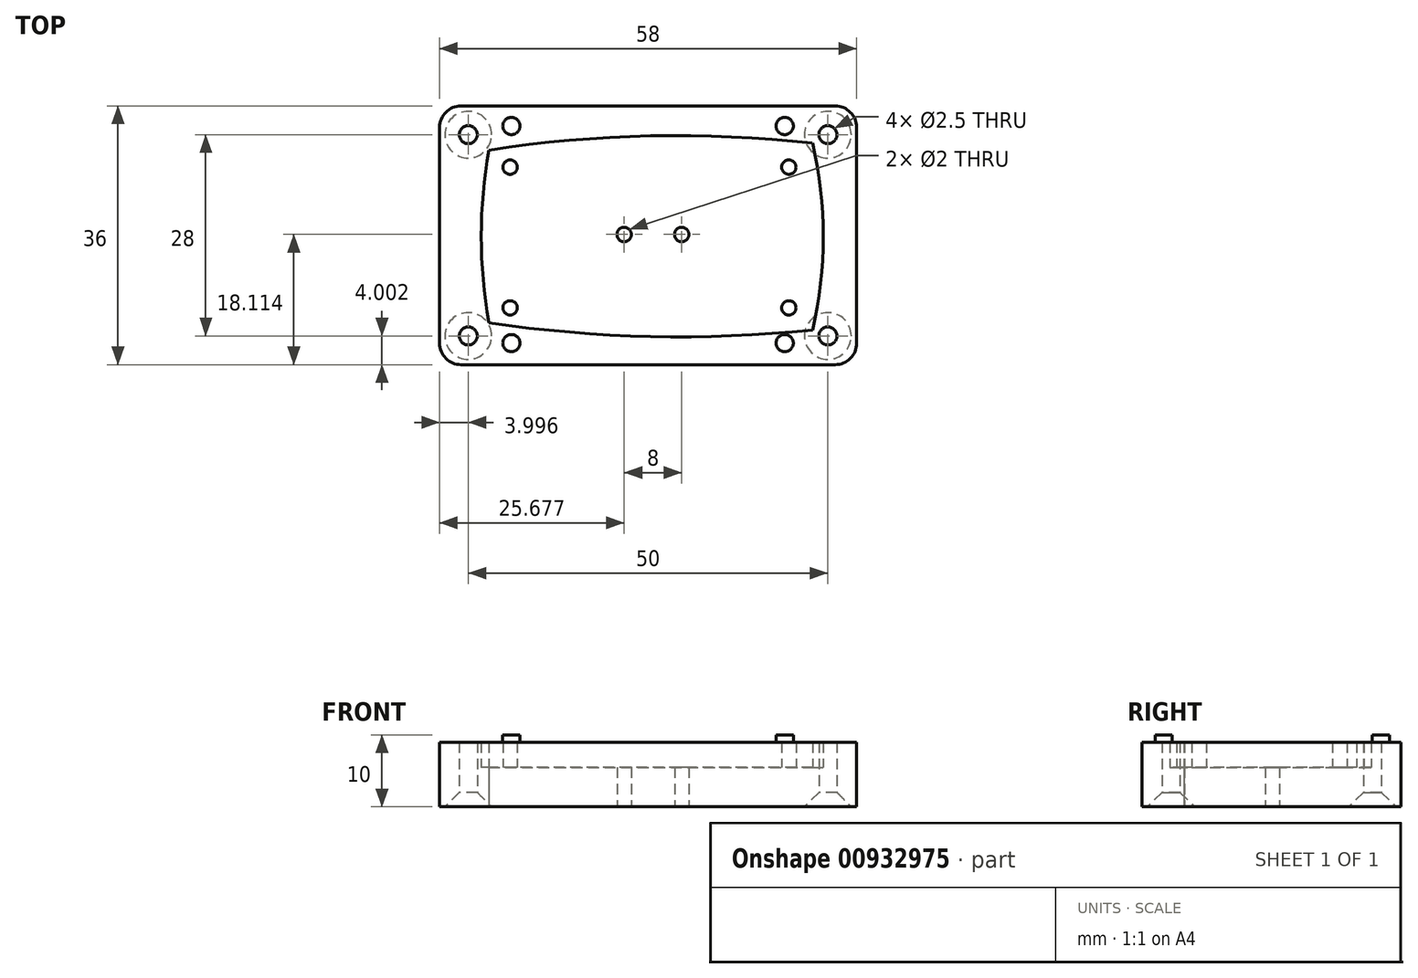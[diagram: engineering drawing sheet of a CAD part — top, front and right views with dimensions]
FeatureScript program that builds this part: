
annotation { "Feature Type Name" : "Feature", "Feature Type Description" : "" }
export const myFeature = defineFeature(function(context is Context, id is Id, definition is map)
    precondition{}
    {
        {
            var Q0;
            Q0=qCreatedBy(makeId("Top.planeOp"),FACE);
            var sketch = newSketch(context, id + "F0", { "sketchPlane" : qUnion([Q0])});
            skLineSegment(sketch, "E0", {"start": v(-0.01, 0.02) * mm, "end": v(-0.01, 24.02) * mm});
            skLineSegment(sketch, "E1", {"start": v(44.98, -1) * mm, "end": v(44.98, 25) * mm});
            skLineSegment(sketch, "E2", {"start": v(-0.01, 24.02) * mm, "end": v(44.98, 25) * mm});
            skLineSegment(sketch, "E3", {"start": v(-0.01, 0.02) * mm, "end": v(44.98, -1) * mm});
            skArc(sketch, "E4", {"start": v(44.98, 25) * mm, "mid": v(22.45, 26.01) * mm, "end": v(-0.01, 24.02) * mm});
            skArc(sketch, "E5", {"start": v(0, 0) * mm, "mid": v(22.46, -1.9) * mm, "end": v(44.98, -1) * mm});
            skArc(sketch, "E6", {"start": v(44.98, -1) * mm, "mid": v(46.47, 12) * mm, "end": v(44.98, 25) * mm});
            skArc(sketch, "E7", {"start": v(-0.01, 24.02) * mm, "mid": v(-1.07, 12.01) * mm, "end": v(0, 0) * mm});
            skCircle(sketch, "E8", {"center": v(2.94, 21.67) * mm, "radius": 1 * mm});
            skCircle(sketch, "E9", {"center": v(2.94, 2.08) * mm, "radius": 1 * mm});
            skCircle(sketch, "E10", {"center": v(41.7, 2.08) * mm, "radius": 1 * mm});
            skCircle(sketch, "E11", {"center": v(41.7, 21.67) * mm, "radius": 1 * mm});
            skLineSegment(sketch, "E12.bottom", {"start": v(-6.87, 30.18) * mm, "end": v(51.13, 30.18) * mm});
            skLineSegment(sketch, "E12.top", {"start": v(-6.87, -5.82) * mm, "end": v(51.13, -5.82) * mm});
            skLineSegment(sketch, "E12.left", {"start": v(-6.87, 30.18) * mm, "end": v(-6.87, -5.82) * mm});
            skLineSegment(sketch, "E12.right", {"start": v(51.13, 30.18) * mm, "end": v(51.13, -5.82) * mm});
            skCircle(sketch, "E13", {"center": v(-2.87, 26.18) * mm, "radius": 1.25 * mm});
            skCircle(sketch, "E14", {"center": v(-2.87, -1.82) * mm, "radius": 1.25 * mm});
            skCircle(sketch, "E15", {"center": v(47.13, 26.18) * mm, "radius": 1.25 * mm});
            skCircle(sketch, "E16", {"center": v(47.13, -1.82) * mm, "radius": 1.25 * mm});
            skCircle(sketch, "E17", {"center": v(18.8, 12.3) * mm, "radius": 1 * mm});
            skCircle(sketch, "E18", {"center": v(26.8, 12.3) * mm, "radius": 1 * mm});
            skCircle(sketch, "E19", {"center": v(3.13, 27.38) * mm, "radius": 1.2 * mm});
            skCircle(sketch, "E20", {"center": v(41.13, 27.38) * mm, "radius": 1.2 * mm});
            skCircle(sketch, "E21", {"center": v(3.13, -2.82) * mm, "radius": 1.2 * mm});
            skCircle(sketch, "E22", {"center": v(41.13, -2.82) * mm, "radius": 1.2 * mm});
            skSolve(sketch);
        }
        {
            var Q0;
            {var subQ1=sQuery(id+"F0.wireOp",EDGE,"E4");Q0=makeQuery(id+"F0.imprint","IMPRINT",FACE,{"disambiguationData":[TD([[makeQuery(id+"F0.imprint","IMPRINT",EDGE,{"derivedFrom":subQ1}),-1.0]])]});}
            extrude(context, id + "F1", {"entities" : qUnion([Q0]), "depth" : 9 * mm, "offsetDistance" : 25 * mm});
        }
        {
            var Q0;
            {var subQ1=sQuery(id+"F0.wireOp",EDGE,"E1");Q0=makeQuery(id+"F0.imprint","IMPRINT",FACE,{"disambiguationData":[TD([[makeQuery(id+"F0.imprint","IMPRINT",EDGE,{"derivedFrom":subQ1}),1.0]])]});}
            var Q1;
            Q1=makeQuery(id+"F0.imprint","IMPRINT",FACE,{"disambiguationData":[TD([[makeQuery(id+"F0.imprint","IMPRINT",EDGE,{"derivedFrom":sQuery(id+"F0.wireOp",EDGE,"E8")}),1.0]])]});
            var Q2;
            Q2=makeQuery(id+"F0.imprint","IMPRINT",FACE,{"disambiguationData":[TD([[makeQuery(id+"F0.imprint","IMPRINT",EDGE,{"derivedFrom":sQuery(id+"F0.wireOp",EDGE,"E9")}),1.0]])]});
            var Q3;
            Q3=makeQuery(id+"F0.imprint","IMPRINT",FACE,{"disambiguationData":[TD([[makeQuery(id+"F0.imprint","IMPRINT",EDGE,{"derivedFrom":sQuery(id+"F0.wireOp",EDGE,"E10")}),1.0]])]});
            var Q4;
            Q4=makeQuery(id+"F0.imprint","IMPRINT",FACE,{"disambiguationData":[TD([[makeQuery(id+"F0.imprint","IMPRINT",EDGE,{"derivedFrom":sQuery(id+"F0.wireOp",EDGE,"E11")}),1.0]])]});
            var Q5;
            Q5=makeQuery(id+"F0.imprint","IMPRINT",FACE,{"disambiguationData":[TD([[makeQuery(id+"F0.imprint","IMPRINT",EDGE,{"derivedFrom":sQuery(id+"F0.wireOp",EDGE,"E2")}),1.0]])]});
            var Q6;
            {var subQ0=sQuery(id+"F0.wireOp",EDGE,"E5");Q6=makeQuery(id+"F0.imprint","IMPRINT",FACE,{"disambiguationData":[TD([[makeQuery(id+"F0.imprint","IMPRINT",EDGE,{"derivedFrom":subQ0}),1.0]])]});}
            var Q7;
            Q7=makeQuery(id+"F0.imprint","IMPRINT",FACE,{"disambiguationData":[TD([[makeQuery(id+"F0.imprint","IMPRINT",EDGE,{"derivedFrom":sQuery(id+"F0.wireOp",EDGE,"E1")}),-1.0]])]});
            var Q8;
            {var subQ0=sQuery(id+"F0.wireOp",EDGE,"E7");var subQ1=sQuery(id+"F0.wireOp",EDGE,"E0");var subQ3=makeQuery(id+"F0.imprint","INTERSECT",VERTEX,{"derivedFrom":[subQ1,subQ0]});Q8=makeQuery(id+"F0.imprint","IMPRINT",FACE,{"disambiguationData":[TD([[makeQuery(id+"F0.imprint","IMPRINT",EDGE,{"disambiguationData":[TD([[subQ3,-1.0]])],"derivedFrom":subQ1}),1.0]])]});}
            extrude(context, id + "F2", {"entities" : qUnion([Q0, Q1, Q2, Q3, Q4, Q5, Q6, Q7, Q8]), "operationType" : NewBodyOperationType.ADD, "depth" : 5.5 * mm, "offsetDistance" : 25 * mm});
        }
        {
            var Q0;
            Q0=makeQuery(id+"F0.imprint","IMPRINT",FACE,{"disambiguationData":[TD([[makeQuery(id+"F0.imprint","IMPRINT",EDGE,{"derivedFrom":sQuery(id+"F0.wireOp",EDGE,"E11")}),1.0]])]});
            var Q1;
            Q1=makeQuery(id+"F0.imprint","IMPRINT",FACE,{"disambiguationData":[TD([[makeQuery(id+"F0.imprint","IMPRINT",EDGE,{"derivedFrom":sQuery(id+"F0.wireOp",EDGE,"E8")}),1.0]])]});
            var Q2;
            Q2=makeQuery(id+"F0.imprint","IMPRINT",FACE,{"disambiguationData":[TD([[makeQuery(id+"F0.imprint","IMPRINT",EDGE,{"derivedFrom":sQuery(id+"F0.wireOp",EDGE,"E9")}),1.0]])]});
            var Q3;
            Q3=makeQuery(id+"F0.imprint","IMPRINT",FACE,{"disambiguationData":[TD([[makeQuery(id+"F0.imprint","IMPRINT",EDGE,{"derivedFrom":sQuery(id+"F0.wireOp",EDGE,"E10")}),1.0]])]});
            extrude(context, id + "F3", {"entities" : qUnion([Q0, Q1, Q2, Q3]), "operationType" : NewBodyOperationType.ADD, "depth" : 9 * mm, "offsetDistance" : 25 * mm});
        }
        {
            var Q0;
            Q0=makeQuery(id+"F1.opExtrude","SWEPT_EDGE",EDGE,{"disambiguationData":[OSD([sQuery(id+"F0.wireOp",EDGE,"E12.bottom"),sQuery(id+"F0.wireOp",EDGE,"E12.right")])]});
            var Q1;
            Q1=makeQuery(id+"F1.opExtrude","SWEPT_EDGE",EDGE,{"disambiguationData":[OSD([sQuery(id+"F0.wireOp",EDGE,"E12.top"),sQuery(id+"F0.wireOp",EDGE,"E12.right")])]});
            var Q2;
            Q2=makeQuery(id+"F1.opExtrude","SWEPT_EDGE",EDGE,{"disambiguationData":[OSD([sQuery(id+"F0.wireOp",EDGE,"E12.top"),sQuery(id+"F0.wireOp",EDGE,"E12.left")])]});
            var Q3;
            Q3=makeQuery(id+"F1.opExtrude","SWEPT_EDGE",EDGE,{"disambiguationData":[OSD([sQuery(id+"F0.wireOp",EDGE,"E12.bottom"),sQuery(id+"F0.wireOp",EDGE,"E12.left")])]});
            fillet(context, id + "F4", {"entities" : qUnion([Q0, Q1, Q2, Q3]), "radius" : 3 * mm, "tangentPropagation" : true, "allowEdgeOverflow" : false});
        }
        {
            var Q0;
            Q0=makeQuery(id+"F1.opExtrude","CAP_EDGE",EDGE,{"disambiguationData":[OSD([sQuery(id+"F0.wireOp",EDGE,"E14")])],"isStart":true});
            var Q1;
            Q1=makeQuery(id+"F1.opExtrude","CAP_EDGE",EDGE,{"disambiguationData":[OSD([sQuery(id+"F0.wireOp",EDGE,"E13")])],"isStart":true});
            var Q2;
            Q2=makeQuery(id+"F1.opExtrude","CAP_EDGE",EDGE,{"disambiguationData":[OSD([sQuery(id+"F0.wireOp",EDGE,"E16")])],"isStart":true});
            var Q3;
            Q3=makeQuery(id+"F1.opExtrude","CAP_EDGE",EDGE,{"disambiguationData":[OSD([sQuery(id+"F0.wireOp",EDGE,"E15")])],"isStart":true});
            chamfer(context, id + "F5", {"entities" : qUnion([Q0, Q1, Q2, Q3]), "width" : 2 * mm, "tangentPropagation" : true});
        }
        {
            var Q0;
            Q0=makeQuery(id+"F0.imprint","IMPRINT",FACE,{"disambiguationData":[TD([[makeQuery(id+"F0.imprint","IMPRINT",EDGE,{"derivedFrom":sQuery(id+"F0.wireOp",EDGE,"E19")}),1.0]])]});
            var Q1;
            Q1=makeQuery(id+"F0.imprint","IMPRINT",FACE,{"disambiguationData":[TD([[makeQuery(id+"F0.imprint","IMPRINT",EDGE,{"derivedFrom":sQuery(id+"F0.wireOp",EDGE,"E21")}),1.0]])]});
            var Q2;
            Q2=makeQuery(id+"F0.imprint","IMPRINT",FACE,{"disambiguationData":[TD([[makeQuery(id+"F0.imprint","IMPRINT",EDGE,{"derivedFrom":sQuery(id+"F0.wireOp",EDGE,"E22")}),1.0]])]});
            var Q3;
            Q3=makeQuery(id+"F0.imprint","IMPRINT",FACE,{"disambiguationData":[TD([[makeQuery(id+"F0.imprint","IMPRINT",EDGE,{"derivedFrom":sQuery(id+"F0.wireOp",EDGE,"E20")}),1.0]])]});
            extrude(context, id + "F6", {"entities" : qUnion([Q0, Q1, Q2, Q3]), "operationType" : NewBodyOperationType.ADD, "depth" : 10 * mm, "offsetDistance" : 25 * mm});
        }
    });
